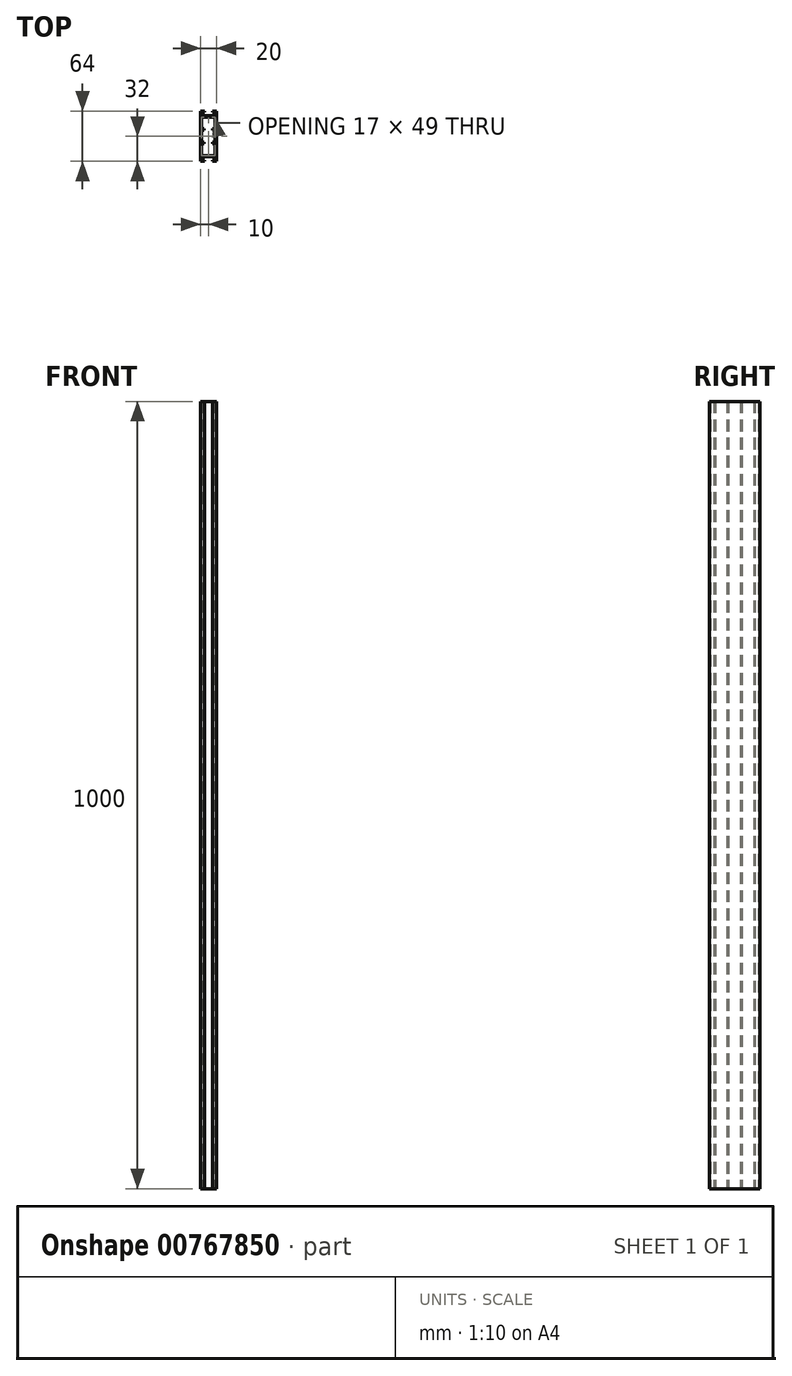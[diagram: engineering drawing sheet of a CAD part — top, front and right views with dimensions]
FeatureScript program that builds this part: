
annotation { "Feature Type Name" : "Feature", "Feature Type Description" : "" }
export const myFeature = defineFeature(function(context is Context, id is Id, definition is map)
    precondition{}
    {
        {
            var Q0;
            Q0=qCreatedBy(makeId("Top.planeOp"),FACE);
            var sketch = newSketch(context, id + "F0", { "sketchPlane" : qUnion([Q0])});
            skLineSegment(sketch, "E0", {"start": v(-5, 32) * mm, "end": v(-10, 32) * mm});
            skLineSegment(sketch, "E1", {"start": v(-10, 32) * mm, "end": v(-10, -32) * mm});
            skLineSegment(sketch, "E2", {"start": v(-10, -32) * mm, "end": v(-5, -32) * mm});
            skLineSegment(sketch, "E3", {"start": v(-5, -32) * mm, "end": v(-5, -30.5) * mm});
            skLineSegment(sketch, "E4", {"start": v(-5, -30.5) * mm, "end": v(-8.5, -30.5) * mm});
            skLineSegment(sketch, "E5", {"start": v(-8.5, -30.5) * mm, "end": v(-8.5, -26) * mm});
            skLineSegment(sketch, "E6", {"start": v(-8.5, -26) * mm, "end": v(8.5, -26) * mm});
            skLineSegment(sketch, "E7", {"start": v(8.5, -26) * mm, "end": v(8.5, -30.5) * mm});
            skLineSegment(sketch, "E8", {"start": v(8.5, -30.5) * mm, "end": v(5, -30.5) * mm});
            skLineSegment(sketch, "E9", {"start": v(5, -30.5) * mm, "end": v(5, -32) * mm});
            skLineSegment(sketch, "E10", {"start": v(5, -32) * mm, "end": v(10, -32) * mm});
            skLineSegment(sketch, "E11", {"start": v(10, -32) * mm, "end": v(10, 32) * mm});
            skLineSegment(sketch, "E12", {"start": v(10, 32) * mm, "end": v(5, 32) * mm});
            skLineSegment(sketch, "E13", {"start": v(5, 32) * mm, "end": v(5, 30.5) * mm});
            skLineSegment(sketch, "E14", {"start": v(5, 30.5) * mm, "end": v(8.5, 30.5) * mm});
            skLineSegment(sketch, "E15", {"start": v(8.5, 30.5) * mm, "end": v(8.5, 26) * mm});
            skLineSegment(sketch, "E16", {"start": v(8.5, 26) * mm, "end": v(-8.5, 26) * mm});
            skLineSegment(sketch, "E17", {"start": v(-8.5, 26) * mm, "end": v(-8.5, 30.5) * mm});
            skLineSegment(sketch, "E18", {"start": v(-8.5, 30.5) * mm, "end": v(-5, 30.5) * mm});
            skLineSegment(sketch, "E19", {"start": v(-5, 30.5) * mm, "end": v(-5, 32) * mm});
            skLineSegment(sketch, "E20", {"start": v(-8.5, 24.5) * mm, "end": v(-8.5, 9.5) * mm});
            skLineSegment(sketch, "E21", {"start": v(-8.5, 9.5) * mm, "end": v(-5.5, 9.5) * mm});
            skLineSegment(sketch, "E22", {"start": v(-5.5, 9.5) * mm, "end": v(-5.5, 7.5) * mm});
            skLineSegment(sketch, "E23", {"start": v(-5.5, 7.5) * mm, "end": v(-8.5, 7.5) * mm});
            skLineSegment(sketch, "E24", {"start": v(-8.5, 7.5) * mm, "end": v(-8.5, -7.5) * mm});
            skLineSegment(sketch, "E25", {"start": v(-8.5, -7.5) * mm, "end": v(-5.5, -7.5) * mm});
            skLineSegment(sketch, "E26", {"start": v(-5.5, -7.5) * mm, "end": v(-5.5, -9.5) * mm});
            skLineSegment(sketch, "E27", {"start": v(-5.5, -9.5) * mm, "end": v(-8.5, -9.5) * mm});
            skLineSegment(sketch, "E28", {"start": v(-8.5, -9.5) * mm, "end": v(-8.5, -24.5) * mm});
            skLineSegment(sketch, "E29", {"start": v(-8.5, -24.5) * mm, "end": v(8.5, -24.5) * mm});
            skLineSegment(sketch, "E30", {"start": v(8.5, -24.5) * mm, "end": v(8.5, -9.5) * mm});
            skLineSegment(sketch, "E31", {"start": v(8.5, -9.5) * mm, "end": v(5.5, -9.5) * mm});
            skLineSegment(sketch, "E32", {"start": v(5.5, -9.5) * mm, "end": v(5.5, -7.5) * mm});
            skLineSegment(sketch, "E33", {"start": v(5.5, -7.5) * mm, "end": v(8.5, -7.5) * mm});
            skLineSegment(sketch, "E34", {"start": v(8.5, -7.5) * mm, "end": v(8.5, 7.5) * mm});
            skLineSegment(sketch, "E35", {"start": v(8.5, 7.5) * mm, "end": v(5.5, 7.5) * mm});
            skLineSegment(sketch, "E36", {"start": v(5.5, 7.5) * mm, "end": v(5.5, 9.5) * mm});
            skLineSegment(sketch, "E37", {"start": v(5.5, 9.5) * mm, "end": v(8.5, 9.5) * mm});
            skLineSegment(sketch, "E38", {"start": v(8.5, 9.5) * mm, "end": v(8.5, 24.5) * mm});
            skLineSegment(sketch, "E39", {"start": v(8.5, 24.5) * mm, "end": v(-8.5, 24.5) * mm});
            skLineSegment(sketch, "E40", {"start": v(0, 26) * mm, "end": v(0, -26) * mm, "construction": true});
            skSolve(sketch);
        }
        {
            var Q0;
            Q0=makeQuery(id+"F0.imprint","IMPRINT",FACE,{"disambiguationData":[TD([[makeQuery(id+"F0.imprint","IMPRINT",EDGE,{"derivedFrom":sQuery(id+"F0.wireOp",EDGE,"E0")}),1.0]])]});
            extrude(context, id + "F1", {"entities" : qUnion([Q0]), "depth" : 1000 * mm, "offsetDistance" : 25 * mm});
        }
    });
